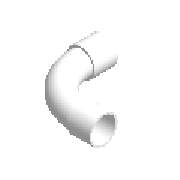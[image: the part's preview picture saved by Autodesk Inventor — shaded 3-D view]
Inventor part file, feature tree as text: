
AUTODESK INVENTOR PART (.ipt)
format: ipt  version: 2023.2 (Build 272271030, 271C)  size: 220,160 bytes
history: native  units: mm (DEFAULTED — no unit token found)
features: other x6, sketch x2, revolve x1
ambient origin geometry x8: Origin, YZ Plane, XZ Plane, XY Plane, X Axis, Y Axis, Z Axis, Center Point
bodies: Solid1 (feature_tree)
feature tree (9):
  sketch  "Sketch1"  dims[d3=90.0deg d0=40.0mm]
  revolve  "Revolution1"  [1 undecoded]
  other  "Work Point18"
  other  "Work Point19"
  other  "Work Axis30"
  other  "Work Point20"
  other  "Work Axis31"
  other  "Work Point21"
  sketch  "Sketch2"  dims[d1=3.0mm d2=26.0mm d4=34.0mm d5=0.0mm d6=40.0mm d7=34.0mm d8=77.0mm d9=77.0mm d160=90.0deg d10=3.0mm d11=3.0mm d12=26.0mm d13=40.0mm d14=80.0mm d15=80.0mm d16=3.0mm d192=0.0mm]
note: 1 required parameter value undecoded (feature->parameter linkage not recoverable at this tier; creation-order binding heuristic only, values carry confidence <= 0.55)
